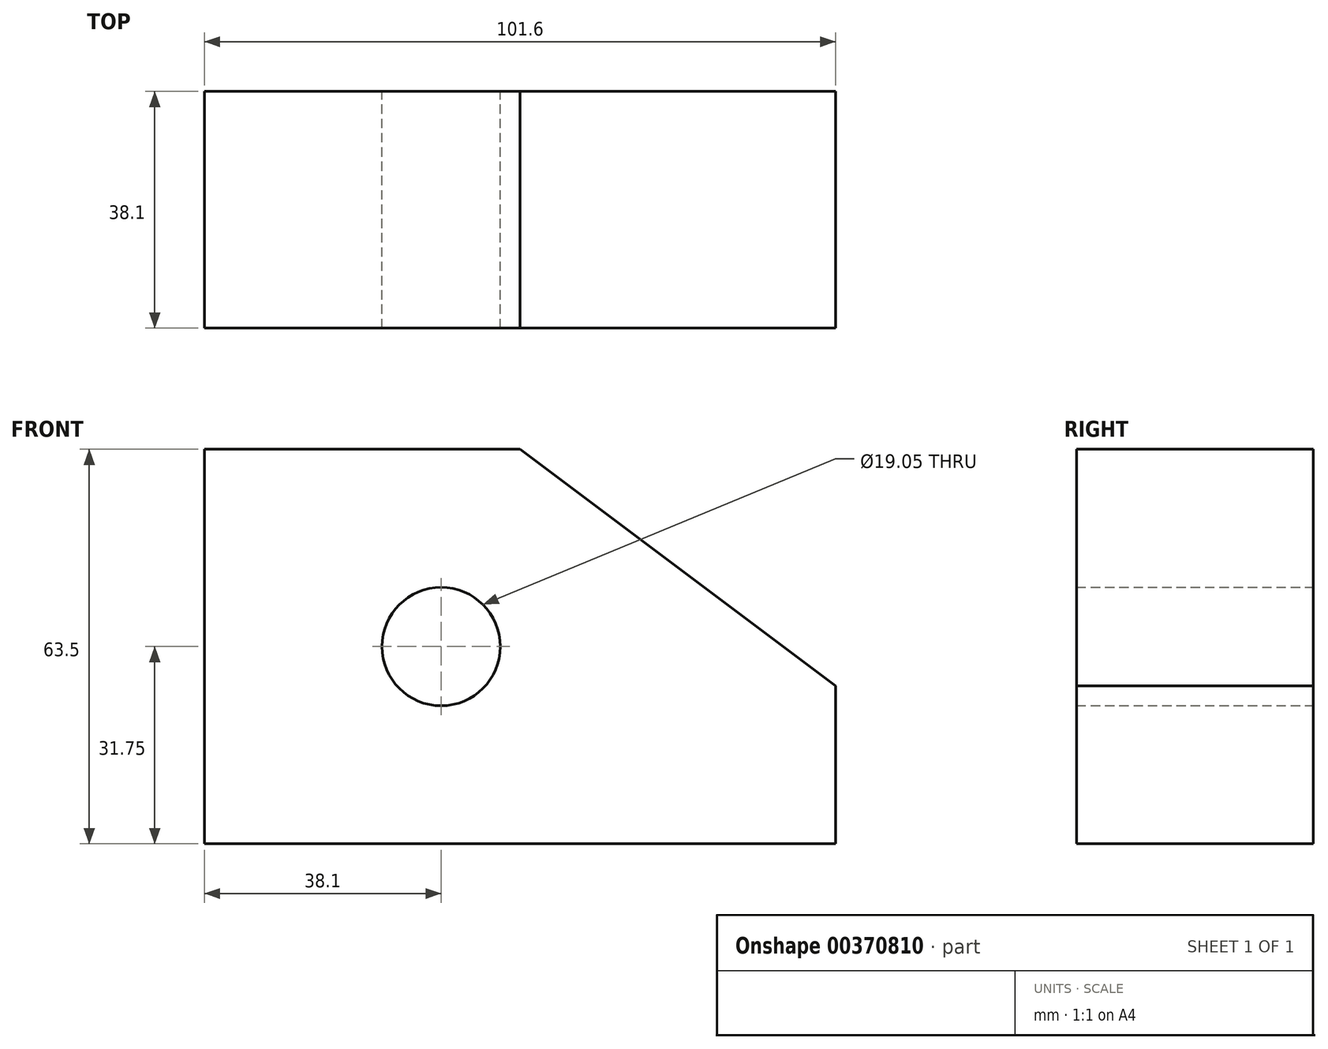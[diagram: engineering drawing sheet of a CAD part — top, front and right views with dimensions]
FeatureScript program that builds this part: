
annotation { "Feature Type Name" : "Feature", "Feature Type Description" : "" }
export const myFeature = defineFeature(function(context is Context, id is Id, definition is map)
    precondition{}
    {
        {
            var Q0;
            Q0=qCreatedBy(makeId("Front.planeOp"),FACE);
            var sketch = newSketch(context, id + "F0", { "sketchPlane" : qUnion([Q0])});
            skLineSegment(sketch, "E0", {"start": v(0, 0) * mm, "end": v(101.6, 0) * mm});
            skLineSegment(sketch, "E1", {"start": v(101.6, 0) * mm, "end": v(101.6, 25.4) * mm});
            skLineSegment(sketch, "E2", {"start": v(101.6, 25.4) * mm, "end": v(50.8, 63.5) * mm});
            skLineSegment(sketch, "E3", {"start": v(50.8, 63.5) * mm, "end": v(0, 63.5) * mm});
            skLineSegment(sketch, "E4", {"start": v(0, 63.5) * mm, "end": v(0, 0) * mm});
            skCircle(sketch, "E5", {"center": v(38.1, 31.75) * mm, "radius": 9.53 * mm});
            skSolve(sketch);
        }
        {
            var Q0;
            Q0=makeQuery(id+"F0.imprint","IMPRINT",FACE,{"disambiguationData":[TD([[makeQuery(id+"F0.imprint","IMPRINT",EDGE,{"derivedFrom":sQuery(id+"F0.wireOp",EDGE,"E0")}),1.0]])]});
            extrude(context, id + "F1", {"entities" : qUnion([Q0]), "depth" : 38.1 * mm});
        }
    });
